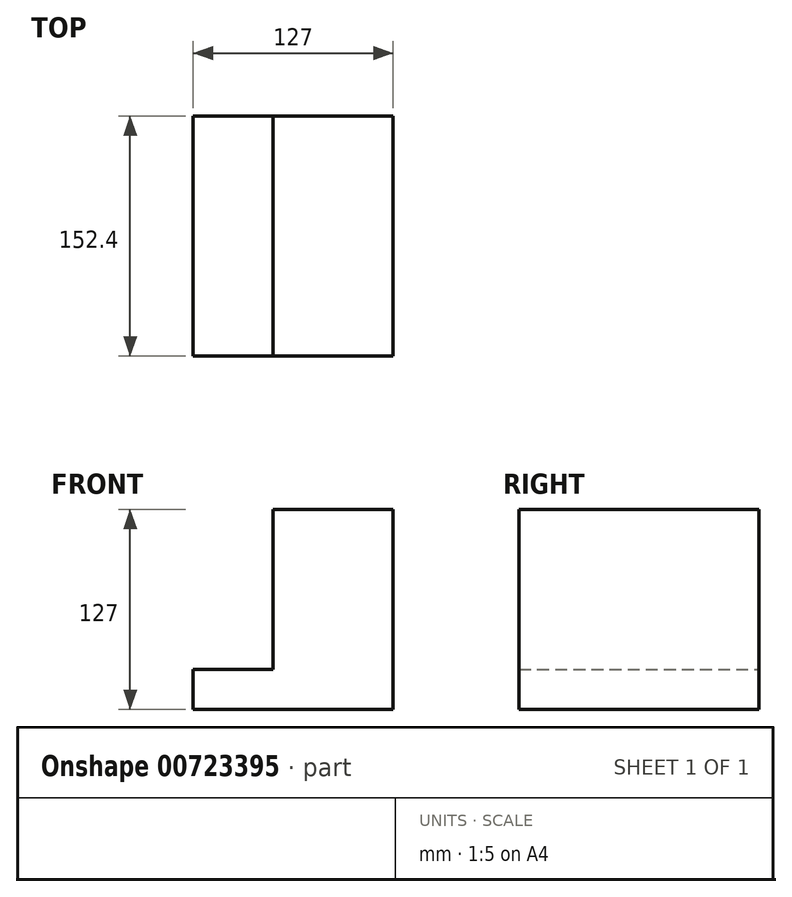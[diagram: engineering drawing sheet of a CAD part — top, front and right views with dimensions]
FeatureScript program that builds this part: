
annotation { "Feature Type Name" : "Feature", "Feature Type Description" : "" }
export const myFeature = defineFeature(function(context is Context, id is Id, definition is map)
    precondition{}
    {
        {
            var Q0;
            Q0=qCreatedBy(makeId("Front.planeOp"),FACE);
            var sketch = newSketch(context, id + "F0", { "sketchPlane" : qUnion([Q0])});
            skLineSegment(sketch, "E0", {"start": v(-76.94, -49.25) * mm, "end": v(-76.94, -74.65) * mm});
            skLineSegment(sketch, "E1", {"start": v(-76.94, -74.65) * mm, "end": v(50.06, -74.65) * mm});
            skLineSegment(sketch, "E2", {"start": v(50.06, -74.65) * mm, "end": v(50.06, 52.35) * mm});
            skLineSegment(sketch, "E3", {"start": v(50.06, 52.35) * mm, "end": v(-26.14, 52.35) * mm});
            skLineSegment(sketch, "E4", {"start": v(-26.14, 52.35) * mm, "end": v(-26.14, -49.25) * mm});
            skLineSegment(sketch, "E5", {"start": v(-26.14, -49.25) * mm, "end": v(-76.94, -49.25) * mm});
            skSolve(sketch);
        }
        {
            var Q0;
            Q0=makeQuery(id+"F0.imprint","IMPRINT",FACE,{"disambiguationData":[TD([[makeQuery(id+"F0.imprint","IMPRINT",EDGE,{"derivedFrom":sQuery(id+"F0.wireOp",EDGE,"E0")}),1.0]])]});
            extrude(context, id + "F1", {"entities" : qUnion([Q0]), "depth" : 152.4 * mm, "offsetDistance" : 25.4 * mm});
        }
    });
